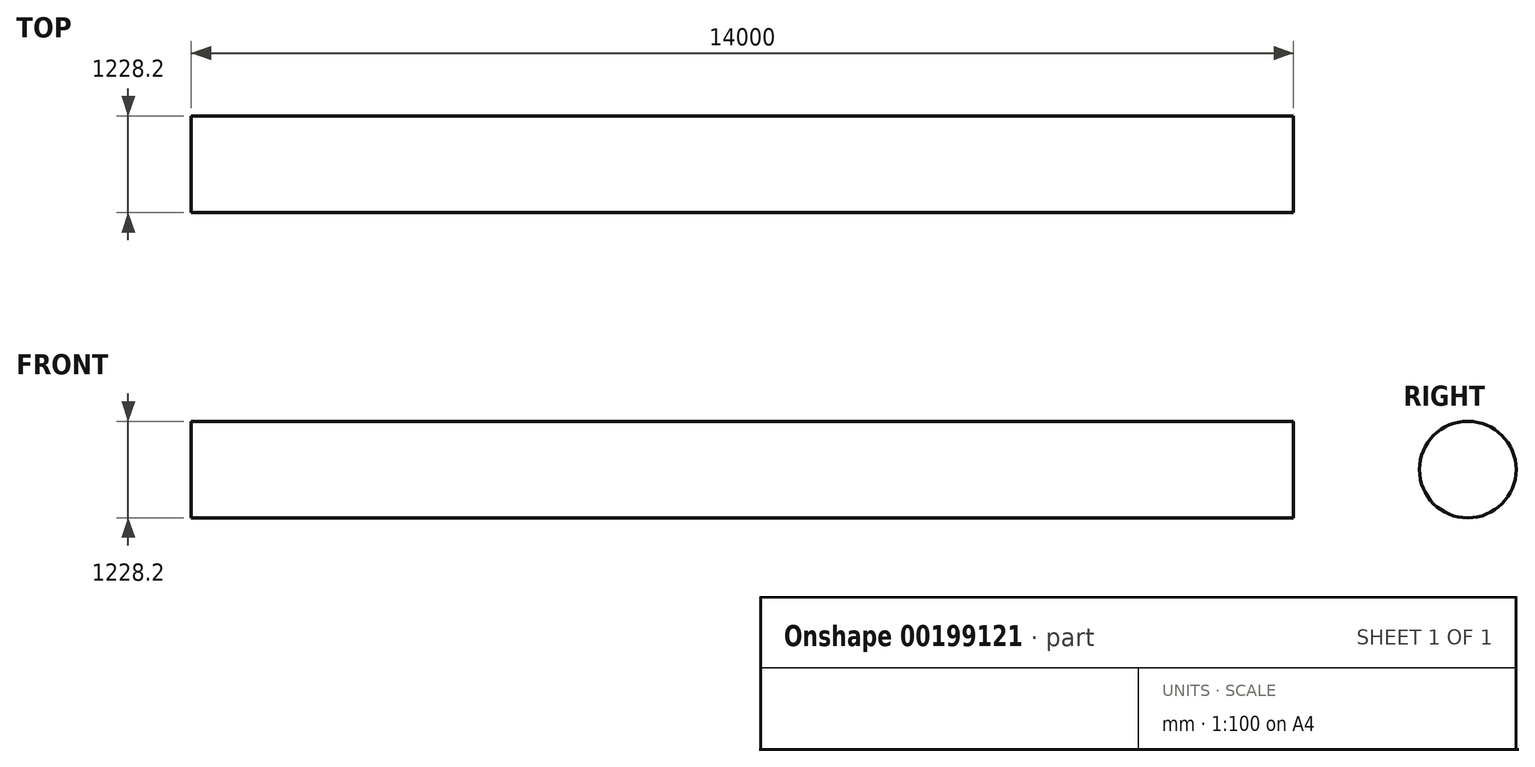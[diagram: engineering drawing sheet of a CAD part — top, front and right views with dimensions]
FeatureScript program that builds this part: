
annotation { "Feature Type Name" : "Feature", "Feature Type Description" : "" }
export const myFeature = defineFeature(function(context is Context, id is Id, definition is map)
    precondition{}
    {
        {
            var Q0;
            Q0=qCreatedBy(makeId("Right.planeOp"),FACE);
            var sketch = newSketch(context, id + "F0", { "sketchPlane" : qUnion([Q0])});
            skCircle(sketch, "E0", {"center": v(0, 0) * mm, "radius": 614.1 * mm});
            skSolve(sketch);
        }
        {
            var Q0;
            Q0 = qSketchRegion(id + "F0", true);
            extrude(context, id + "F1", {"entities" : qUnion([Q0]), "endBound" : BoundingType.SYMMETRIC, "depth" : 14000 * mm});
        }
    });
